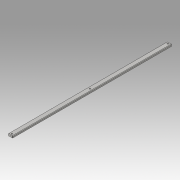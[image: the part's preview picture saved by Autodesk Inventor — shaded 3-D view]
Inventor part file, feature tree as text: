
AUTODESK INVENTOR PART (.ipt)
format: ipt  version: 2016 (Build 200138000, 138)  size: 105,984 bytes
history: native  units: in
note: dims shown in document units (in); Inventor stores cm internally (conversion verified against a paired STEP export)
features: sketch x2, extrude x1, chamfer x1, hole x1
ambient origin geometry x8: Origin, YZ Plane, XZ Plane, XY Plane, X Axis, Y Axis, Z Axis, Center Point
bodies: Solid1 (feature_tree)
feature tree (5):
  extrude  "Extrusion1"  Depth=0.25in
  chamfer  "Chamfer2"  Distance=17.5in
  hole  "Hole1"  [1 undecoded]
  sketch  "Sketch1"  dims[d0=0.5in d1=0.25in d2=17.5in d3=0.0in]
  sketch  "Sketch3"  dims[d14=0.05in d15=0.125in d16=45.0deg d17=0.2in d18=0.15in d19=0.2in d20=0.15in d21=0.2in d22=8.7in d23=0.15in d24=0.75in d25=0.375in d26=0.25in d27=0.5635in d28=1.0in d29=0.8108in]
note: 1 required parameter value undecoded (feature->parameter linkage not recoverable at this tier; creation-order binding heuristic only, values carry confidence <= 0.55)
